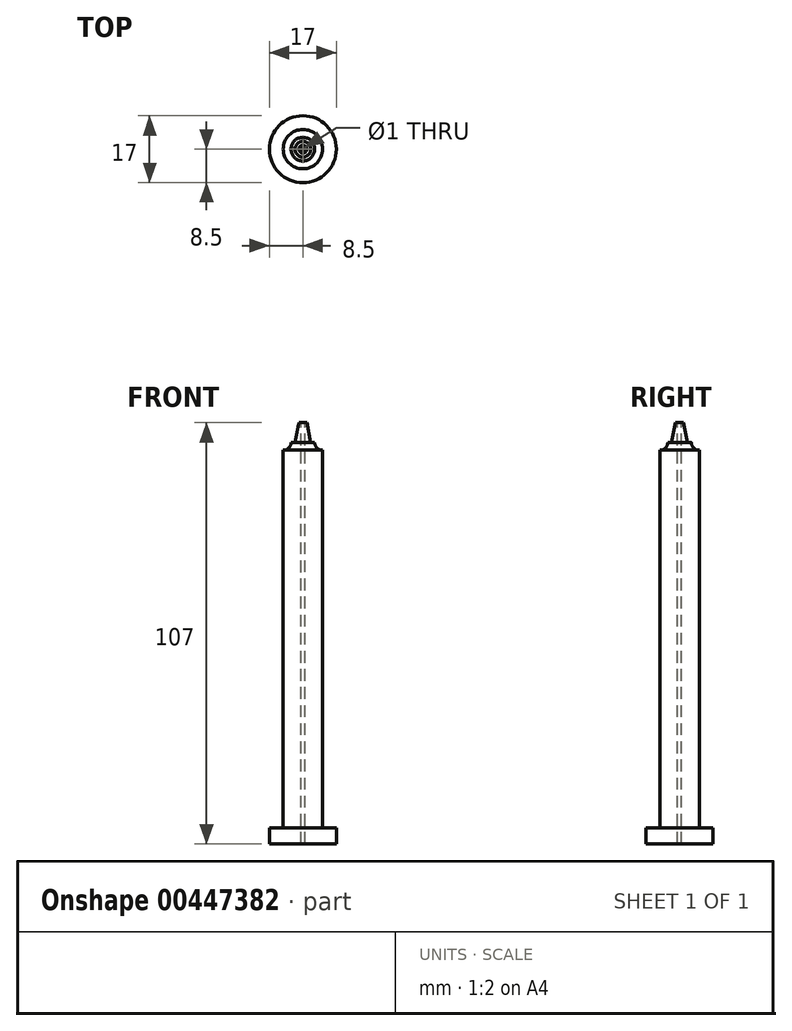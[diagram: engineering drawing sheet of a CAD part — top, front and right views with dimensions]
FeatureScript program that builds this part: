
annotation { "Feature Type Name" : "Feature", "Feature Type Description" : "" }
export const myFeature = defineFeature(function(context is Context, id is Id, definition is map)
    precondition{}
    {
        {
            var Q0;
            Q0=qCreatedBy(makeId("Top.planeOp"),FACE);
            var sketch = newSketch(context, id + "F0", { "sketchPlane" : qUnion([Q0])});
            skCircle(sketch, "E0", {"center": v(0, 0) * mm, "radius": 8.5 * mm});
            skSolve(sketch);
        }
        {
            var Q0;
            Q0=qSketchRegion(id+"F0",true);
            extrude(context, id + "F1", {"entities" : qUnion([Q0]), "depth" : 4 * mm});
        }
        {
            var Q0;
            Q0=qCreatedBy(makeId("Top.planeOp"),FACE);
            var sketch = newSketch(context, id + "F2", { "sketchPlane" : qUnion([Q0])});
            skCircle(sketch, "E1", {"center": v(0, 0) * mm, "radius": 5 * mm});
            skSolve(sketch);
        }
        {
            var Q0;
            Q0=qSketchRegion(id+"F2",true);
            extrude(context, id + "F3", {"entities" : qUnion([Q0]), "operationType" : NewBodyOperationType.ADD, "depth" : 100 * mm});
        }
        {
            var Q0;
            Q0=qCreatedBy(makeId("Right.planeOp"),FACE);
            var sketch = newSketch(context, id + "F4", { "sketchPlane" : qUnion([Q0])});
            skLineSegment(sketch, "E2", {"start": v(0, 102) * mm, "end": v(0, 100) * mm});
            skLineSegment(sketch, "E3", {"start": v(0, 100) * mm, "end": v(5, 100) * mm});
            skLineSegment(sketch, "E4", {"start": v(3, 102) * mm, "end": v(0, 102) * mm});
            skArc(sketch, "E5", {"start": v(3, 102) * mm, "mid": v(3.59, 100.59) * mm, "end": v(5, 100) * mm});
            skSolve(sketch);
        }
        {
            var Q0;
            Q0=makeQuery(id+"F4.imprint","IMPRINT",FACE,{"disambiguationData":[TD([[makeQuery(id+"F4.imprint","IMPRINT",EDGE,{"derivedFrom":sQuery(id+"F4.wireOp",EDGE,"E2")}),1.0]])]});
            var Q1;
            Q1=sQuery(id+"F4.wireOp",EDGE,"E2");
            revolve(context, id + "F5", {"operationType" : NewBodyOperationType.ADD, "entities" : qUnion([Q0]), "axis" : qUnion([Q1]), "revolveType" : RevolveType.FULL});
        }
        {
            var Q0;
            Q0=qCreatedBy(makeId("Right.planeOp"),FACE);
            var sketch = newSketch(context, id + "F6", { "sketchPlane" : qUnion([Q0])});
            skLineSegment(sketch, "E6", {"start": v(0, 102) * mm, "end": v(0, 107) * mm});
            skLineSegment(sketch, "E7", {"start": v(0, 107) * mm, "end": v(1, 107) * mm});
            skLineSegment(sketch, "E8", {"start": v(1, 107) * mm, "end": v(2, 102) * mm});
            skLineSegment(sketch, "E9", {"start": v(2, 102) * mm, "end": v(0, 102) * mm});
            skSolve(sketch);
        }
        {
            var Q0;
            Q0=makeQuery(id+"F6.imprint","IMPRINT",FACE,{"disambiguationData":[TD([[makeQuery(id+"F6.imprint","IMPRINT",EDGE,{"derivedFrom":sQuery(id+"F6.wireOp",EDGE,"E6")}),-1.0]])]});
            var Q1;
            Q1=sQuery(id+"F6.wireOp",EDGE,"E6");
            revolve(context, id + "F7", {"operationType" : NewBodyOperationType.ADD, "entities" : qUnion([Q0]), "axis" : qUnion([Q1]), "revolveType" : RevolveType.FULL});
        }
        {
            var Q0;
            Q0=makeQuery(id+"F7.opRevolve","SWEPT_FACE",FACE,{"disambiguationData":[OSD([sQuery(id+"F6.wireOp",EDGE,"E7")])]});
            var sketch = newSketch(context, id + "F8", { "sketchPlane" : qUnion([Q0])});
            skCircle(sketch, "E10", {"center": v(0, 0) * mm, "radius": 0.5 * mm});
            skSolve(sketch);
        }
        {
            var Q0;
            Q0 = qSketchRegion(id + "F8", true);
            extrude(context, id + "F9", {"entities" : qUnion([Q0]), "operationType" : NewBodyOperationType.REMOVE, "oppositeDirection" : true, "depth" : 129.4 * mm});
        }
    });
